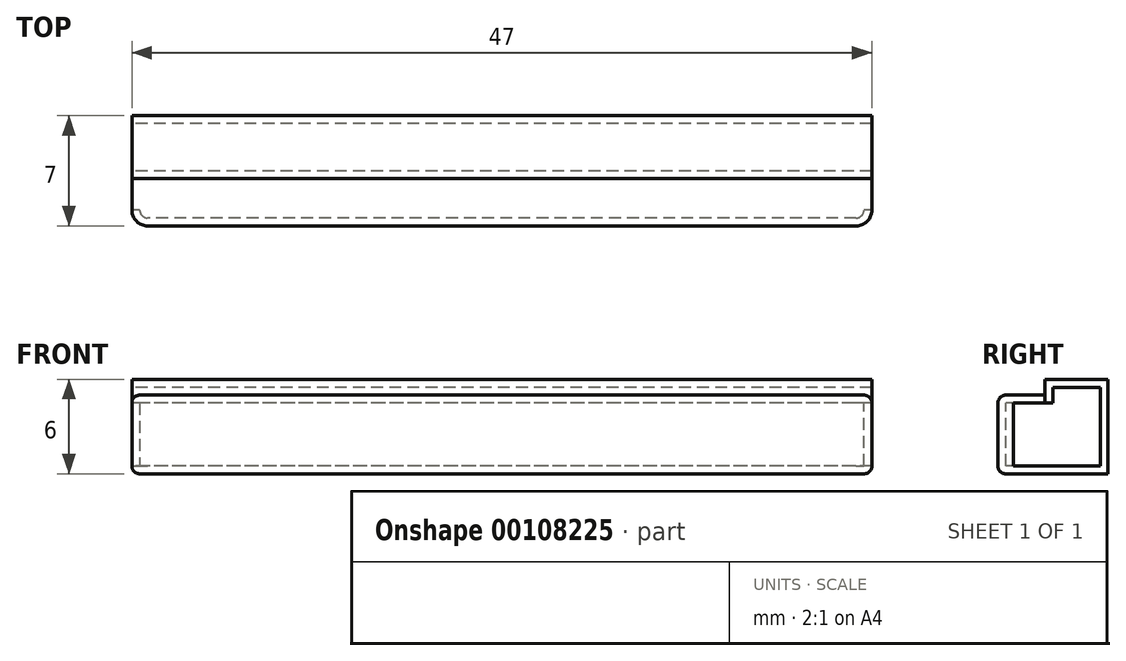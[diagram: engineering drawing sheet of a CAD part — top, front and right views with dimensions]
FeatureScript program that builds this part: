
annotation { "Feature Type Name" : "Feature", "Feature Type Description" : "" }
export const myFeature = defineFeature(function(context is Context, id is Id, definition is map)
    precondition{}
    {
        {
            var Q0;
            Q0=qCreatedBy(makeId("Right.planeOp"),FACE);
            var sketch = newSketch(context, id + "F0", { "sketchPlane" : qUnion([Q0])});
            skLineSegment(sketch, "E0", {"start": v(0, 0) * mm, "end": v(7, 0) * mm});
            skLineSegment(sketch, "E1", {"start": v(7, 0) * mm, "end": v(7, 6) * mm});
            skLineSegment(sketch, "E2", {"start": v(7, 6) * mm, "end": v(3, 6) * mm});
            skLineSegment(sketch, "E3", {"start": v(3, 6) * mm, "end": v(3, 5) * mm});
            skLineSegment(sketch, "E4", {"start": v(3, 5) * mm, "end": v(0, 5) * mm});
            skLineSegment(sketch, "E5", {"start": v(0, 5) * mm, "end": v(0, 0) * mm});
            skSolve(sketch);
        }
        {
            var Q0;
            Q0 = qSketchRegion(id + "F0", true);
            extrude(context, id + "F1", {"entities" : qUnion([Q0]), "endBound" : BoundingType.SYMMETRIC, "depth" : 47 * mm});
        }
        {
            var Q0;
            Q0=makeQuery(id+"F1.opExtrude","CAP_EDGE",EDGE,{"disambiguationData":[OSD([sQuery(id+"F0.wireOp",EDGE,"E5")])],"isStart":false});
            var Q1;
            Q1=makeQuery(id+"F1.opExtrude","CAP_EDGE",EDGE,{"disambiguationData":[OSD([sQuery(id+"F0.wireOp",EDGE,"E5")])],"isStart":true});
            fillet(context, id + "F2", {"entities" : qUnion([Q0, Q1]), "radius" : 1 * mm, "tangentPropagation" : true, "allowEdgeOverflow" : false});
        }
        {
            var Q0;
            Q0=makeQuery(id+"F1.opExtrude","SWEPT_EDGE",EDGE,{"disambiguationData":[OSD([sQuery(id+"F0.wireOp",EDGE,"E4"),sQuery(id+"F0.wireOp",EDGE,"E5")])]});
            var Q1;
            Q1=makeQuery(id+"F1.opExtrude","SWEPT_EDGE",EDGE,{"disambiguationData":[OSD([sQuery(id+"F0.wireOp",EDGE,"E0"),sQuery(id+"F0.wireOp",EDGE,"E5")])]});
            fillet(context, id + "F3", {"entities" : qUnion([Q0, Q1]), "radius" : 0.5 * mm, "tangentPropagation" : true, "allowEdgeOverflow" : false});
        }
        {
            var Q0;
            Q0=makeQuery(id+"F1.opExtrude","CAP_FACE",FACE,{"disambiguationData":[OSD([sQuery(id+"F0.wireOp",EDGE,"E0"),sQuery(id+"F0.wireOp",EDGE,"E1"),sQuery(id+"F0.wireOp",EDGE,"E2"),sQuery(id+"F0.wireOp",EDGE,"E3"),sQuery(id+"F0.wireOp",EDGE,"E4"),sQuery(id+"F0.wireOp",EDGE,"E5")])],"isStart":false});
            var Q1;
            Q1=makeQuery(id+"F1.opExtrude","CAP_FACE",FACE,{"disambiguationData":[OSD([sQuery(id+"F0.wireOp",EDGE,"E0"),sQuery(id+"F0.wireOp",EDGE,"E1"),sQuery(id+"F0.wireOp",EDGE,"E2"),sQuery(id+"F0.wireOp",EDGE,"E3"),sQuery(id+"F0.wireOp",EDGE,"E4"),sQuery(id+"F0.wireOp",EDGE,"E5")])],"isStart":true});
            shell(context, id + "F4", {"entities" : qUnion([Q0, Q1]), "thickness" : 0.5 * mm});
        }
    });
